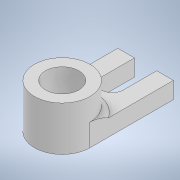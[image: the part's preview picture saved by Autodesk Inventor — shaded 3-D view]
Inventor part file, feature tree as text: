
AUTODESK INVENTOR PART (.ipt)
format: ipt  version: 2020 (Build 240168000, 168)  size: 137,728 bytes
history: native  units: mm
features: sketch x5, extrude x4, hole x1, fillet x1, chamfer x1, projected_geometry x1
ambient origin geometry x8: Origin, YZ Plane, XZ Plane, XY Plane, X Axis, Y Axis, Z Axis, Center Point
bodies: Solid1 (feature_tree)
feature tree (13):
  extrude  "Extrusion1"  Depth=50.0mm
  extrude  "Extrusion2"  Depth=40.0mm TaperAngle=0.0deg
  extrude  "Extrusion3"  TaperAngle=0.0deg  [1 undecoded]
  hole  "Hole1"  [1 undecoded]
  extrude  "Extrusion4"  Depth=10.0mm TaperAngle=0.0deg
  fillet  "Fillet1"  Radius=5.0mm
  chamfer  "Chamfer1"  Distance=5.0mm Angle=45.0deg
  sketch  "Sketch1"  dims[d0=75.0mm d1=50.0mm]
  sketch  "Sketch2"  dims[d2=15.0mm d3=0.0mm d4=40.0mm d5=0.0mm]
  sketch  "Sketch3"  dims[d6=30.0mm d7=0.0mm d8=0.0mm]
  sketch  "Sketch4"  dims[d9=30.0mm d10=25.0mm]
  sketch  "Sketch5"  dims[d11=20.0mm d12=6.0mm d13=4.0mm d14=2.0mm d15=90.0deg d16=8.0mm d17=20.594885mm d18=10.0mm d19=0.0mm d20=5.0mm d22=5.0mm d23=2.0mm d24=45.0deg]
  projected_geometry  "Projected Loop1"
note: 2 required parameter values undecoded (feature->parameter linkage not recoverable at this tier; creation-order binding heuristic only, values carry confidence <= 0.55)
